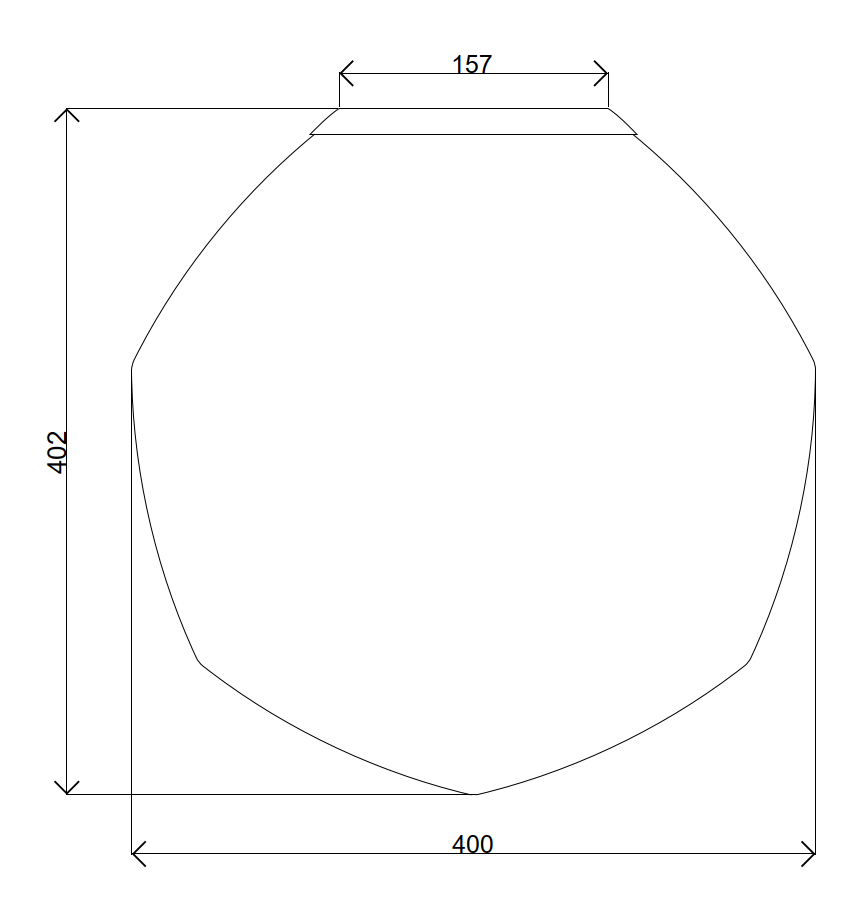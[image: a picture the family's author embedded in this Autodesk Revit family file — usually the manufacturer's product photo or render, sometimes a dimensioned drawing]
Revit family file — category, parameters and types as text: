
# Revit family: 63_UN_Pendant_Cloak Canopy_Signify
name_source: partatom
category: Lighting Fixtures
units: mm (PartAtom-declared; Revit-internal decimal feet)

## family parameters
Always vertical = Yes
Cut with Voids When Loaded = No
Light Source = Yes
OmniClass Number = 23.80.70.11
OmniClass Title = Luminaries for Internal Lighting
Part Type = Normal
Room Calculation Point = Yes
Round Connector Dimension = Use Diameter
Shared = No
Work Plane-Based = No

## types (1)
- Cloak Canopy
    Apparent Load = 10 VA
    Assembly Code = 63.0
    Color Filter = 16777215
    Dimming Lamp Color Temperature Shift = <None>
    IfcExportAs = IfcLightFixtureType
    IfcExportType = USERDEFINED
    Lamp = LED
    Light Source Symbol Size = 610 mm
    Manufacturer = Signify
    Model = Pendant Track
    Pendant_Material = UHMW, White
    Type Comments = Cloak
    URL = https://www.signify.com
    Voltage = 230 V
    Wattage Comments = 10W

## geometry (parser evidence)
native form markers: Sweep x7
no freeform markers — native parametric forms only
